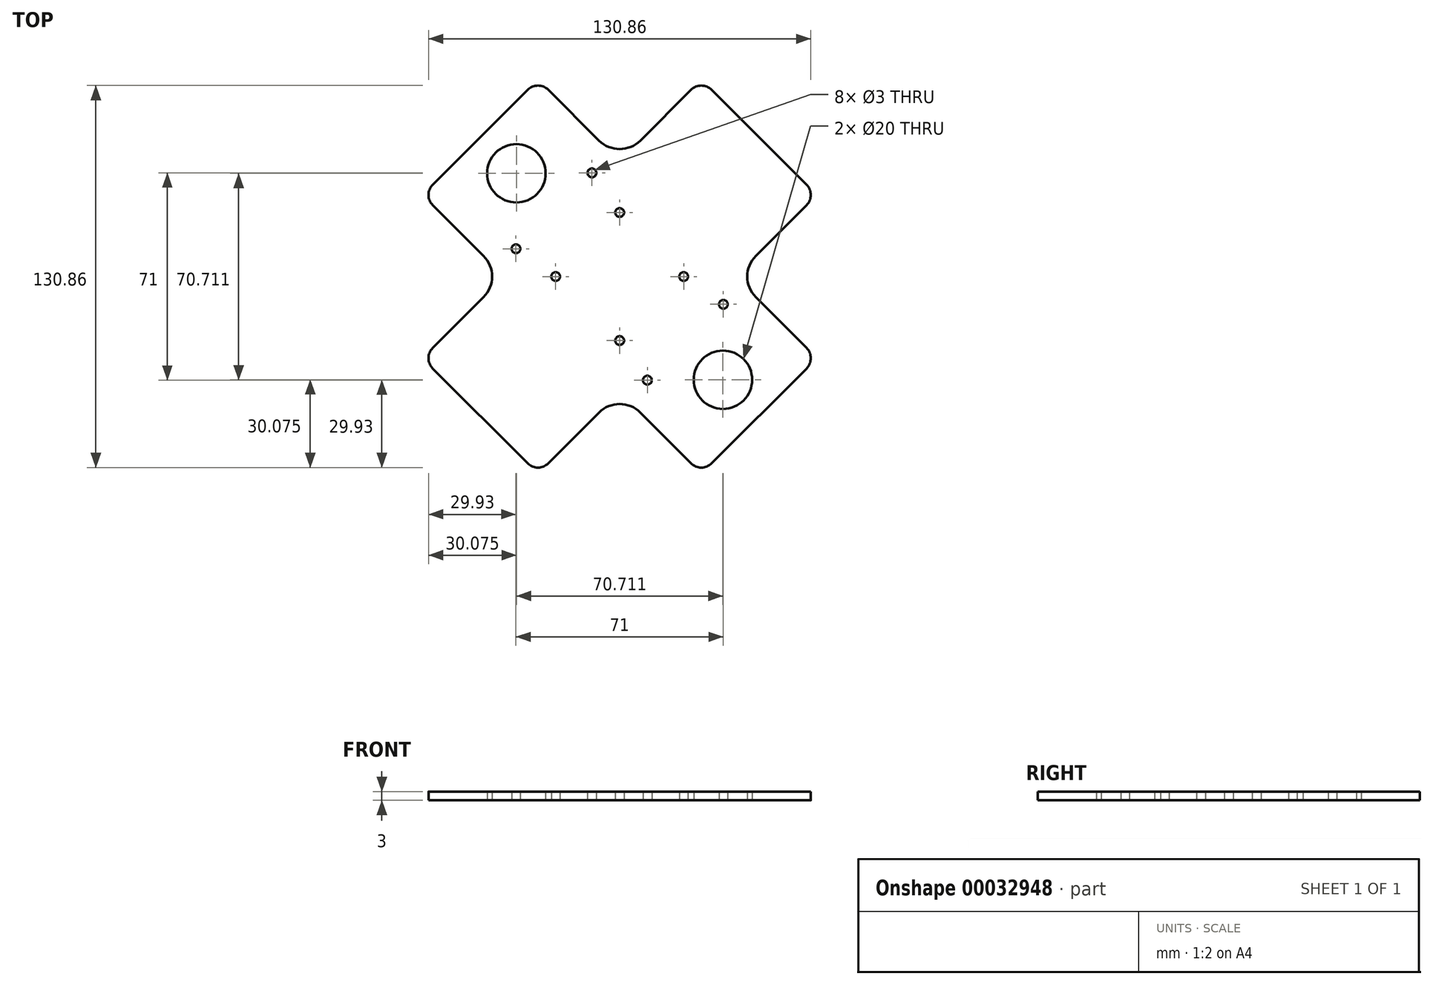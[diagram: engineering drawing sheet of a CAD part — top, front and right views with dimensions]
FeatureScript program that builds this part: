
annotation { "Feature Type Name" : "Feature", "Feature Type Description" : "" }
export const myFeature = defineFeature(function(context is Context, id is Id, definition is map)
    precondition{}
    {
        {
            var Q0;
            Q0=qCreatedBy(makeId("Top.planeOp"),FACE);
            var sketch = newSketch(context, id + "F0", { "sketchPlane" : qUnion([Q0])});
            skLineSegment(sketch, "E0", {"start": v(0, 67.5) * mm, "end": v(0, -67.5) * mm, "construction": true});
            skLineSegment(sketch, "E1", {"start": v(-67.5, 0) * mm, "end": v(67.5, 0) * mm, "construction": true});
            skLineSegment(sketch, "E2", {"start": v(0, 0) * mm, "end": v(95.46, 0) * mm, "construction": true});
            skLineSegment(sketch, "E3.MirrorCS", {"start": v(0, 0) * mm, "end": v(0, 95.46) * mm, "construction": true});
            skLineSegment(sketch, "E4", {"start": v(27.96, 67.5) * mm, "end": v(67.5, 27.96) * mm});
            skLineSegment(sketch, "E5.MirrorCS", {"start": v(-67.5, -27.96) * mm, "end": v(-27.96, -67.5) * mm});
            skLineSegment(sketch, "E6.MirrorCS", {"start": v(-27.96, 67.5) * mm, "end": v(-67.5, 27.96) * mm});
            skLineSegment(sketch, "E7.MirrorCS", {"start": v(27.96, -67.5) * mm, "end": v(67.5, -27.96) * mm});
            skPoint(sketch, "E8.orphan", {"position": v(0, 95.46) * mm});
            skPoint(sketch, "E9.orphan", {"position": v(95.46, 0) * mm});
            skPoint(sketch, "E10.orphan", {"position": v(0, -95.46) * mm});
            skPoint(sketch, "E11.orphan", {"position": v(-95.46, 0) * mm});
            skLineSegment(sketch, "E12", {"start": v(54.5, 9.5) * mm, "end": v(-9.5, -54.5) * mm, "construction": true});
            skLineSegment(sketch, "E13", {"start": v(54.5, -9.5) * mm, "end": v(-54.5, -9.5) * mm, "construction": true});
            skCircle(sketch, "E14", {"center": v(35.5, -9.5) * mm, "radius": 1.5 * mm});
            skLineSegment(sketch, "E15", {"start": v(-47.73, 47.73) * mm, "end": v(47.73, -47.73) * mm, "construction": true});
            skCircle(sketch, "E16.MirrorC", {"center": v(9.5, -35.5) * mm, "radius": 1.5 * mm});
            skLineSegment(sketch, "E17", {"start": v(47.73, 47.73) * mm, "end": v(-47.73, -47.73) * mm, "construction": true});
            skCircle(sketch, "E18.MirrorC", {"center": v(-9.5, 35.5) * mm, "radius": 1.5 * mm});
            skCircle(sketch, "E19.MirrorC", {"center": v(-35.5, 9.5) * mm, "radius": 1.5 * mm});
            skLineSegment(sketch, "E20", {"start": v(-27.96, 67.5) * mm, "end": v(-7.07, 46.61) * mm});
            skLineSegment(sketch, "E21", {"start": v(7.07, 46.61) * mm, "end": v(27.96, 67.5) * mm});
            skLineSegment(sketch, "E22.1.0", {"start": v(-46.61, 7.07) * mm, "end": v(-67.5, 27.96) * mm});
            skLineSegment(sketch, "E22.1.1", {"start": v(-67.5, -27.96) * mm, "end": v(-46.61, -7.07) * mm});
            skLineSegment(sketch, "E22.2.0", {"start": v(-7.07, -46.61) * mm, "end": v(-27.96, -67.5) * mm});
            skLineSegment(sketch, "E22.2.1", {"start": v(27.96, -67.5) * mm, "end": v(7.07, -46.61) * mm});
            skLineSegment(sketch, "E22.3.0", {"start": v(46.61, -7.07) * mm, "end": v(67.5, -27.96) * mm});
            skLineSegment(sketch, "E22.3.1", {"start": v(67.5, 27.96) * mm, "end": v(46.61, 7.07) * mm});
            skPoint(sketch, "E22.center", {"position": v(0, 0) * mm});
            skPoint(sketch, "E23.visualSharp", {"position": v(0, 39.54) * mm});
            skArc(sketch, "E23.filletArc", {"start": v(-7.07, 46.61) * mm, "mid": v(0, 43.68) * mm, "end": v(7.07, 46.61) * mm});
            skPoint(sketch, "E24.visualSharp", {"position": v(39.54, 0) * mm});
            skArc(sketch, "E24.filletArc", {"start": v(46.61, 7.07) * mm, "mid": v(43.68, 0) * mm, "end": v(46.61, -7.07) * mm});
            skPoint(sketch, "E25.visualSharp", {"position": v(0, -39.54) * mm});
            skArc(sketch, "E25.filletArc", {"start": v(7.07, -46.61) * mm, "mid": v(0, -43.68) * mm, "end": v(-7.07, -46.61) * mm});
            skPoint(sketch, "E26.visualSharp", {"position": v(-39.54, 0) * mm});
            skArc(sketch, "E26.filletArc", {"start": v(-46.61, -7.07) * mm, "mid": v(-43.68, 0) * mm, "end": v(-46.61, 7.07) * mm});
            skCircle(sketch, "E27.cCircle", {"center": v(0, 0) * mm, "radius": 15.5 * mm, "construction": true});
            skLineSegment(sketch, "E27.0", {"start": v(0, 21.92) * mm, "end": v(21.92, 0) * mm, "construction": true});
            skLineSegment(sketch, "E27.1", {"start": v(21.92, 0) * mm, "end": v(0, -21.92) * mm, "construction": true});
            skLineSegment(sketch, "E27.2", {"start": v(0, -21.92) * mm, "end": v(-21.92, 0) * mm, "construction": true});
            skLineSegment(sketch, "E27.3", {"start": v(-21.92, 0) * mm, "end": v(0, 21.92) * mm, "construction": true});
            skPoint(sketch, "E27.0.midPoint", {"position": v(10.96, 10.96) * mm});
            skCircle(sketch, "E28", {"center": v(21.92, 0) * mm, "radius": 1.5 * mm});
            skCircle(sketch, "E29.1.0", {"center": v(0, 21.92) * mm, "radius": 1.5 * mm});
            skCircle(sketch, "E29.2.0", {"center": v(-21.92, 0) * mm, "radius": 1.5 * mm});
            skCircle(sketch, "E29.3.0", {"center": v(0, -21.92) * mm, "radius": 1.5 * mm});
            skCircle(sketch, "E30", {"center": v(35.36, -35.36) * mm, "radius": 10 * mm});
            skCircle(sketch, "E31.MirrorC", {"center": v(-35.36, 35.36) * mm, "radius": 10 * mm});
            skSolve(sketch);
        }
        {
            var Q0;
            Q0=qSketchRegion(id+"F0",true);
            extrude(context, id + "F1", {"entities" : qUnion([Q0]), "depth" : 3 * mm});
        }
        {
            var Q0;
            Q0=makeQuery(id+"F1.opExtrude","SWEPT_EDGE",EDGE,{"disambiguationData":[OSD([sQuery(id+"F0.wireOp",EDGE,"E6.MirrorCS"),sQuery(id+"F0.wireOp",EDGE,"40bda7d8-425d-454f-b8a7-2a1bb9e9c1f30.MirrorCS")])]});
            var Q1;
            Q1=makeQuery(id+"F1.opExtrude","SWEPT_EDGE",EDGE,{"disambiguationData":[OSD([sQuery(id+"F0.wireOp",EDGE,"E6.MirrorCS"),sQuery(id+"F0.wireOp",EDGE,"639fdff6-1b54-4df2-b334-e074c171bda80.MirrorCS")])]});
            var Q2;
            Q2=makeQuery(id+"F1.opExtrude","SWEPT_EDGE",EDGE,{"disambiguationData":[OSD([sQuery(id+"F0.wireOp",EDGE,"E5.MirrorCS"),sQuery(id+"F0.wireOp",EDGE,"639fdff6-1b54-4df2-b334-e074c171bda80.MirrorCS")])]});
            var Q3;
            Q3=makeQuery(id+"F1.opExtrude","SWEPT_EDGE",EDGE,{"disambiguationData":[OSD([sQuery(id+"F0.wireOp",EDGE,"E5.MirrorCS"),sQuery(id+"F0.wireOp",EDGE,"08b10221-03fd-4825-a98c-2e22a12b5e570.MirrorCS")])]});
            var Q4;
            Q4=makeQuery(id+"F1.opExtrude","SWEPT_EDGE",EDGE,{"disambiguationData":[OSD([sQuery(id+"F0.wireOp",EDGE,"E7.MirrorCS"),sQuery(id+"F0.wireOp",EDGE,"08b10221-03fd-4825-a98c-2e22a12b5e570.MirrorCS")])]});
            var Q5;
            Q5=makeQuery(id+"F1.opExtrude","SWEPT_EDGE",EDGE,{"disambiguationData":[OSD([sQuery(id+"F0.wireOp",EDGE,"E7.MirrorCS"),sQuery(id+"F0.wireOp",EDGE,"892458ac-c66e-45d0-8947-92047cfbfc1c")])]});
            var Q6;
            Q6=makeQuery(id+"F1.opExtrude","SWEPT_EDGE",EDGE,{"disambiguationData":[OSD([sQuery(id+"F0.wireOp",EDGE,"E4"),sQuery(id+"F0.wireOp",EDGE,"892458ac-c66e-45d0-8947-92047cfbfc1c")])]});
            var Q7;
            Q7=makeQuery(id+"F1.opExtrude","SWEPT_EDGE",EDGE,{"disambiguationData":[OSD([sQuery(id+"F0.wireOp",EDGE,"E4"),sQuery(id+"F0.wireOp",EDGE,"40bda7d8-425d-454f-b8a7-2a1bb9e9c1f30.MirrorCS")])]});
            fillet(context, id + "F2", {"entities" : qUnion([Q0, Q1, Q2, Q3, Q4, Q5, Q6, Q7]), "radius" : 5 * mm, "tangentPropagation" : true, "allowEdgeOverflow" : false});
        }
    });
